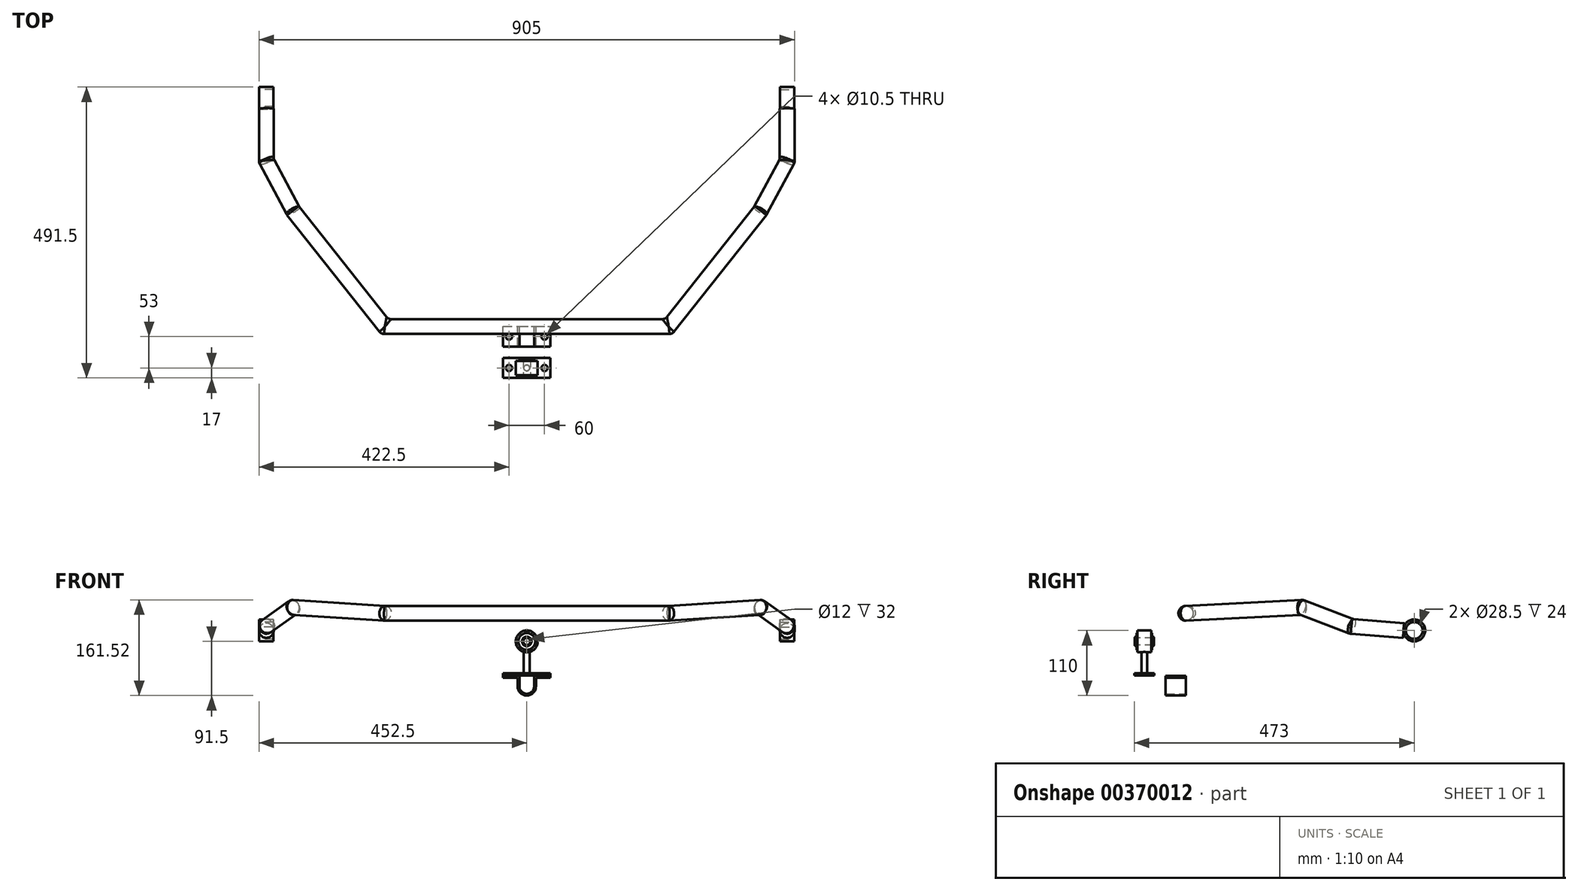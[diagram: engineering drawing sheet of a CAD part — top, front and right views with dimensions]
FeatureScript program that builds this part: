
annotation { "Feature Type Name" : "Feature", "Feature Type Description" : "" }
export const myFeature = defineFeature(function(context is Context, id is Id, definition is map)
    precondition{}
    {
        {
            var Q0;
            Q0=qCreatedBy(makeId("Top.planeOp"),FACE);
            var sketch = newSketch(context, id + "F0", { "sketchPlane" : qUnion([Q0])});
            skLineSegment(sketch, "E0", {"start": v(0, 0) * mm, "end": v(240, 0) * mm, "construction": true});
            skLineSegment(sketch, "E1", {"start": v(0, 0) * mm, "end": v(-240, 0) * mm, "construction": true});
            skLineSegment(sketch, "E2", {"start": v(0, 0) * mm, "end": v(0, 405) * mm, "construction": true});
            skPoint(sketch, "E3", {"position": v(0, 196) * mm});
            skPoint(sketch, "E4", {"position": v(0, 280) * mm});
            skPoint(sketch, "E5", {"position": v(0, 368) * mm});
            skLineSegment(sketch, "E6", {"start": v(0, 196) * mm, "end": v(395, 196) * mm, "construction": true});
            skLineSegment(sketch, "E7", {"start": v(0, 196) * mm, "end": v(-395, 196) * mm, "construction": true});
            skLineSegment(sketch, "E8", {"start": v(0, 368) * mm, "end": v(440, 368) * mm, "construction": true});
            skLineSegment(sketch, "E9", {"start": v(0, 368) * mm, "end": v(-440, 368) * mm, "construction": true});
            skLineSegment(sketch, "E10", {"start": v(395, 196) * mm, "end": v(240, 0) * mm, "construction": true});
            skLineSegment(sketch, "E11", {"start": v(-440, 368) * mm, "end": v(-395, 196) * mm, "construction": true});
            skLineSegment(sketch, "E12", {"start": v(-395, 196) * mm, "end": v(-240, 0) * mm, "construction": true});
            skPoint(sketch, "E13", {"position": v(440, 280) * mm});
            skLineSegment(sketch, "E14", {"start": v(395, 196) * mm, "end": v(440, 280) * mm, "construction": true});
            skLineSegment(sketch, "E15", {"start": v(440, 280) * mm, "end": v(440, 368) * mm, "construction": true});
            skSolve(sketch);
        }
        {
            var Q0;
            Q0=qCreatedBy(makeId("Right.planeOp"),FACE);
            var sketch = newSketch(context, id + "F1", { "sketchPlane" : qUnion([Q0])});
            skLineSegment(sketch, "E16.0", {"start": v(196, 0) * mm, "end": v(0, 0) * mm, "construction": true});
            skPoint(sketch, "E17", {"position": v(0, 47.5) * mm});
            skPoint(sketch, "E18", {"position": v(196, 57.5) * mm});
            skPoint(sketch, "E19", {"position": v(280, 0) * mm});
            skPoint(sketch, "E20", {"position": v(280, 25.5) * mm});
            skPoint(sketch, "E21", {"position": v(368, 0) * mm});
            skLineSegment(sketch, "E22", {"start": v(368, 0) * mm, "end": v(368, 18.5) * mm});
            skLineSegment(sketch, "E23", {"start": v(0, 47.5) * mm, "end": v(196, 57.5) * mm});
            skLineSegment(sketch, "E24", {"start": v(196, 57.5) * mm, "end": v(280, 25.5) * mm});
            skLineSegment(sketch, "E25", {"start": v(368, 18.5) * mm, "end": v(280, 25.5) * mm});
            skLineSegment(sketch, "E26", {"start": v(0, 47.5) * mm, "end": v(0, 0) * mm});
            skLineSegment(sketch, "E27", {"start": v(196, 57.5) * mm, "end": v(196, 0) * mm});
            skLineSegment(sketch, "E28", {"start": v(280, 25.5) * mm, "end": v(280, 0) * mm});
            skSolve(sketch);
        }
        {
            var Q0;
            Q0=qCreatedBy(makeId("Right.planeOp"),FACE);
            cPlane(context, id + "F2", {"entities" : qUnion([Q0]), "cplaneType" : CPlaneType.OFFSET, "offset" : 240 * mm, "width" : 150 * mm, "height" : 150 * mm});
        }
        {
            var Q0;
            Q0=qCreatedBy(id+"F2.planeOp",FACE);
            var sketch = newSketch(context, id + "F3", { "sketchPlane" : qUnion([Q0])});
            skLineSegment(sketch, "E29.0", {"start": v(0, 47.5) * mm, "end": v(0, 0) * mm});
            skSolve(sketch);
        }
        {
            var Q0;
            Q0=sQuery(id+"F3.wireOp",VERTEX,"E29.0.start");
            var Q1;
            Q1=sQuery(id+"F3.wireOp",VERTEX,"E29.0.end");
            var Q2;
            Q2=sQuery(id+"F0.wireOp",VERTEX,"E10.start");
            cPlane(context, id + "F4", {"entities" : qUnion([Q0, Q1, Q2]), "cplaneType" : CPlaneType.THREE_POINT, "offset" : 25 * mm, "width" : 150 * mm, "height" : 150 * mm});
        }
        {
            var Q0;
            Q0=qCreatedBy(id+"F4.planeOp",FACE);
            var sketch = newSketch(context, id + "F5", { "sketchPlane" : qUnion([Q0])});
            skLineSegment(sketch, "E30.0", {"start": v(-148.87, 47.5) * mm, "end": v(-148.87, 0) * mm});
            skLineSegment(sketch, "E31.0", {"start": v(-398.75, 0) * mm, "end": v(-148.87, 0) * mm, "construction": true});
            skLineSegment(sketch, "E32", {"start": v(-398.75, 0) * mm, "end": v(-398.75, 57.5) * mm});
            skLineSegment(sketch, "E33", {"start": v(-398.75, 57.5) * mm, "end": v(-148.87, 47.5) * mm});
            skSolve(sketch);
        }
        {
            var Q0;
            Q0=sQuery(id+"F5.wireOp",VERTEX,"E33.start");
            var Q1;
            Q1=sQuery(id+"F5.wireOp",VERTEX,"E32.start");
            var Q2;
            Q2=sQuery(id+"F0.wireOp",VERTEX,"E13");
            cPlane(context, id + "F6", {"entities" : qUnion([Q0, Q1, Q2]), "cplaneType" : CPlaneType.THREE_POINT, "offset" : 25 * mm, "width" : 150 * mm, "height" : 150 * mm});
        }
        {
            var Q0;
            Q0=qCreatedBy(id+"F6.planeOp",FACE);
            var sketch = newSketch(context, id + "F7", { "sketchPlane" : qUnion([Q0])});
            skLineSegment(sketch, "E34.0", {"start": v(-359.3, 0) * mm, "end": v(-359.3, 57.5) * mm});
            skLineSegment(sketch, "E35.0", {"start": v(-359.3, 0) * mm, "end": v(-454.6, 0) * mm, "construction": true});
            skLineSegment(sketch, "E36", {"start": v(-454.6, 0) * mm, "end": v(-454.6, 25.5) * mm});
            skLineSegment(sketch, "E37", {"start": v(-454.6, 25.5) * mm, "end": v(-359.3, 57.5) * mm});
            skSolve(sketch);
        }
        {
            var Q0;
            Q0=sQuery(id+"F7.wireOp",VERTEX,"E37.start");
            var Q1;
            Q1=sQuery(id+"F0.wireOp",VERTEX,"E13");
            var Q2;
            Q2=sQuery(id+"F0.wireOp",VERTEX,"E15.end");
            cPlane(context, id + "F8", {"entities" : qUnion([Q0, Q1, Q2]), "cplaneType" : CPlaneType.THREE_POINT, "offset" : 25 * mm, "width" : 150 * mm, "height" : 150 * mm});
        }
        {
            var Q0;
            Q0=qCreatedBy(id+"F8.planeOp",FACE);
            var sketch = newSketch(context, id + "F9", { "sketchPlane" : qUnion([Q0])});
            skLineSegment(sketch, "E38.0", {"start": v(-280, 0) * mm, "end": v(-280, 25.5) * mm});
            skLineSegment(sketch, "E39.0", {"start": v(-280, 0) * mm, "end": v(-368, 0) * mm, "construction": true});
            skLineSegment(sketch, "E40", {"start": v(-368, 0) * mm, "end": v(-368, 18.5) * mm});
            skLineSegment(sketch, "E41", {"start": v(-368, 18.5) * mm, "end": v(-280, 25.5) * mm});
            skSolve(sketch);
        }
        {
            var Q0;
            Q0=qCreatedBy(makeId("Front.planeOp"),FACE);
            var sketch = newSketch(context, id + "F10", { "sketchPlane" : qUnion([Q0])});
            skLineSegment(sketch, "E42", {"start": v(0, 0) * mm, "end": v(240, 0) * mm});
            skLineSegment(sketch, "E43.0", {"start": v(0, 47.5) * mm, "end": v(0, 0) * mm});
            skLineSegment(sketch, "E44", {"start": v(0, 47.5) * mm, "end": v(240, 47.5) * mm});
            skSolve(sketch);
        }
        {
            var Q0;
            Q0=qCreatedBy(makeId("Right.planeOp"),FACE);
            var sketch = newSketch(context, id + "F11", { "sketchPlane" : qUnion([Q0])});
            skCircle(sketch, "E45", {"center": v(0, 47.5) * mm, "radius": 12.5 * mm});
            skSolve(sketch);
        }
        {
            var Q0;
            Q0=makeQuery(id+"F11.imprint","IMPRINT",FACE,{"disambiguationData":[TD([[makeQuery(id+"F11.imprint","IMPRINT",EDGE,{"derivedFrom":sQuery(id+"F11.wireOp",EDGE,"E45")}),1.0]])]});
            var Q1;
            Q1=sQuery(id+"F10.wireOp",EDGE,"E44");
            var Q2;
            Q2=sQuery(id+"F5.wireOp",EDGE,"E33");
            var Q3;
            Q3=sQuery(id+"F7.wireOp",EDGE,"E37");
            var Q4;
            Q4=sQuery(id+"F9.wireOp",EDGE,"E41");
            sweep(context, id + "F12", {"profiles" : qUnion([Q0]), "path" : qUnion([Q1, Q2, Q3, Q4])});
        }
        {
            var Q0;
            Q0=qCreatedBy(id+"F8.planeOp",FACE);
            var sketch = newSketch(context, id + "F13", { "sketchPlane" : qUnion([Q0])});
            skLineSegment(sketch, "E46.0", {"start": v(-367, 6.04) * mm, "end": v(-369, 30.96) * mm});
            skPoint(sketch, "E47", {"position": v(-386, 18.5) * mm});
            skPoint(sketch, "E47.positionSnap0", {"position": v(-368, 18.5) * mm});
            skCircle(sketch, "E48", {"center": v(-386, 18.5) * mm, "radius": 18.5 * mm});
            skCircle(sketch, "E49", {"center": v(-386, 18.5) * mm, "radius": 14.25 * mm});
            skSolve(sketch);
        }
        {
            var Q0;
            Q0 = qSketchRegion(id + "F13", true);
            extrude(context, id + "F14", {"entities" : qUnion([Q0]), "operationType" : NewBodyOperationType.ADD, "endBound" : BoundingType.SYMMETRIC, "depth" : 24 * mm});
        }
        {
            var Q0;
            Q0=makeQuery(id+"F12.opSweep","MID_CAP_EDGE",EDGE,{"disambiguationData":[OSD([sQuery(id+"F5.wireOp",VERTEX,"E33.end"),sQuery(id+"F11.wireOp",EDGE,"E45")])],"capPos":1.0});
            var Q1;
            Q1=makeQuery(id+"F12.opSweep","MID_CAP_EDGE",EDGE,{"disambiguationData":[OSD([sQuery(id+"F7.wireOp",VERTEX,"E37.end"),sQuery(id+"F11.wireOp",EDGE,"E45")])],"capPos":2.0});
            var Q2;
            Q2=makeQuery(id+"F12.opSweep","MID_CAP_EDGE",EDGE,{"disambiguationData":[OSD([sQuery(id+"F9.wireOp",VERTEX,"E41.end"),sQuery(id+"F11.wireOp",EDGE,"E45")])],"capPos":3.0});
            fillet(context, id + "F15", {"entities" : qUnion([Q0, Q1, Q2]), "radius" : 10 * mm, "tangentPropagation" : true, "allowEdgeOverflow" : false});
        }
        {
            var Q0;
            Q0=makeQuery(id+"F12.opSweep","SWEPT_BODY",BODY,{"disambiguationData":[OSD([sQuery(id+"F9.wireOp",EDGE,"E41"),sQuery(id+"F11.wireOp",EDGE,"E45")])]});
            var Q1;
            Q1=qCreatedBy(makeId("Right.planeOp"),FACE);
            mirror(context, id + "F16", {"operationType" : NewBodyOperationType.ADD, "entities" : qUnion([Q0]), "mirrorPlane" : qUnion([Q1])});
        }
        {
            var Q0;
            Q0=qCreatedBy(makeId("Front.planeOp"),FACE);
            cPlane(context, id + "F17", {"entities" : qUnion([Q0]), "cplaneType" : CPlaneType.OFFSET, "offset" : 70 * mm, "width" : 150 * mm, "height" : 150 * mm});
        }
        {
            var Q0;
            Q0=qCreatedBy(id+"F17.planeOp",FACE);
            var sketch = newSketch(context, id + "F18", { "sketchPlane" : qUnion([Q0])});
            skCircle(sketch, "E50", {"center": v(0, 0) * mm, "radius": 18.5 * mm});
            skCircle(sketch, "E51", {"center": v(0, 0) * mm, "radius": 14.25 * mm});
            skSolve(sketch);
        }
        {
            var Q0;
            Q0 = qSketchRegion(id + "F18", true);
            extrude(context, id + "F19", {"entities" : qUnion([Q0]), "endBound" : BoundingType.SYMMETRIC, "depth" : 24 * mm});
        }
        {
            var Q0;
            Q0=qCreatedBy(id+"F17.planeOp",FACE);
            var sketch = newSketch(context, id + "F20", { "sketchPlane" : qUnion([Q0])});
            skPoint(sketch, "E52", {"position": v(0, -57.5) * mm});
            skLineSegment(sketch, "E53", {"start": v(0, -57.5) * mm, "end": v(40, -57.5) * mm});
            skLineSegment(sketch, "E54", {"start": v(40, -57.5) * mm, "end": v(40, -53.5) * mm});
            skLineSegment(sketch, "E55", {"start": v(40, -53.5) * mm, "end": v(-40, -53.5) * mm});
            skLineSegment(sketch, "E56", {"start": v(-40, -53.5) * mm, "end": v(-40, -57.5) * mm});
            skLineSegment(sketch, "E57", {"start": v(-40, -57.5) * mm, "end": v(0, -57.5) * mm});
            skSolve(sketch);
        }
        {
            var Q0;
            Q0 = qSketchRegion(id + "F20", true);
            extrude(context, id + "F21", {"entities" : qUnion([Q0]), "endBound" : BoundingType.SYMMETRIC, "depth" : 34 * mm});
        }
        {
            var Q0;
            Q0=qCreatedBy(id+"F17.planeOp",FACE);
            var sketch = newSketch(context, id + "F22", { "sketchPlane" : qUnion([Q0])});
            skCircle(sketch, "E58.0", {"center": v(0, 0) * mm, "radius": 18.5 * mm});
            skPoint(sketch, "E59", {"position": v(0, -18.5) * mm});
            skLineSegment(sketch, "E60.0", {"start": v(40, -53.5) * mm, "end": v(-40, -53.5) * mm});
            skLineSegment(sketch, "E61", {"start": v(0, -18.5) * mm, "end": v(0, -53.5) * mm});
            skLineSegment(sketch, "E62", {"start": v(0, -53.5) * mm, "end": v(5, -53.5) * mm});
            skLineSegment(sketch, "E63", {"start": v(5, -53.5) * mm, "end": v(5, -17.5) * mm});
            skLineSegment(sketch, "E64", {"start": v(5, -17.5) * mm, "end": v(0, -17.5) * mm});
            skLineSegment(sketch, "E65", {"start": v(0, -17.5) * mm, "end": v(0, -18.5) * mm});
            skSolve(sketch);
        }
        {
            var Q0;
            {var subQ0=sQuery(id+"F22.wireOp",EDGE,"E61");Q0=makeQuery(id+"F22.imprint","IMPRINT",FACE,{"disambiguationData":[TD([[makeQuery(id+"F22.imprint","IMPRINT",EDGE,{"derivedFrom":subQ0}),1.0]])]});}
            var Q1;
            Q1=sQuery(id+"F22.wireOp",EDGE,"E61");
            revolve(context, id + "F23", {"operationType" : NewBodyOperationType.ADD, "entities" : qUnion([Q0]), "axis" : qUnion([Q1]), "revolveType" : RevolveType.FULL});
        }
        {
            var Q0;
            Q0=qCreatedBy(makeId("Right.planeOp"),FACE);
            var sketch = newSketch(context, id + "F24", { "sketchPlane" : qUnion([Q0])});
            skLineSegment(sketch, "E66.0", {"start": v(-82, -14.25) * mm, "end": v(-82, 14.25) * mm});
            skLineSegment(sketch, "E67", {"start": v(-82, 0) * mm, "end": v(-57, 0) * mm});
            skPoint(sketch, "E67.endSnap0", {"position": v(-82, 0) * mm});
            skLineSegment(sketch, "E68", {"start": v(-57, 0) * mm, "end": v(-57, 14.25) * mm});
            skLineSegment(sketch, "E69", {"start": v(-57, 14.25) * mm, "end": v(-83, 14.25) * mm});
            skLineSegment(sketch, "E70", {"start": v(-83, 14.25) * mm, "end": v(-83, 0) * mm});
            skLineSegment(sketch, "E71", {"start": v(-83, 0) * mm, "end": v(-82, 0) * mm});
            skPoint(sketch, "E72", {"position": v(-70, 0) * mm});
            skPoint(sketch, "E72.positionSnap0", {"position": v(-70, 14.25) * mm});
            skLineSegment(sketch, "E73", {"start": v(-70, 0) * mm, "end": v(-86, 0) * mm});
            skLineSegment(sketch, "E74", {"start": v(-86, 0) * mm, "end": v(-86, 6) * mm});
            skLineSegment(sketch, "E75", {"start": v(-86, 6) * mm, "end": v(-54, 6) * mm});
            skLineSegment(sketch, "E76", {"start": v(-54, 6) * mm, "end": v(-54, 0) * mm});
            skLineSegment(sketch, "E77", {"start": v(-54, 0) * mm, "end": v(-57, 0) * mm});
            skLineSegment(sketch, "E78", {"start": v(-86, 6) * mm, "end": v(-86, 8) * mm});
            skLineSegment(sketch, "E79", {"start": v(-86, 8) * mm, "end": v(-83, 8) * mm});
            skLineSegment(sketch, "E80", {"start": v(-54, 6) * mm, "end": v(-54, 8) * mm});
            skLineSegment(sketch, "E81", {"start": v(-54, 8) * mm, "end": v(-57, 8) * mm});
            skSolve(sketch);
        }
        {
            var Q0;
            {var subQ4=sQuery(id+"F24.wireOp",EDGE,"E80");Q0=makeQuery(id+"F24.imprint","IMPRINT",FACE,{"disambiguationData":[TD([[makeQuery(id+"F24.imprint","IMPRINT",EDGE,{"derivedFrom":subQ4}),1.0]])]});}
            var Q1;
            {var subQ4=sQuery(id+"F24.wireOp",EDGE,"E78");Q1=makeQuery(id+"F24.imprint","IMPRINT",FACE,{"disambiguationData":[TD([[makeQuery(id+"F24.imprint","IMPRINT",EDGE,{"derivedFrom":subQ4}),-1.0]])]});}
            var Q2;
            {var subQ0=sQuery(id+"F24.wireOp",EDGE,"E69");var subQ6=sQuery(id+"F24.wireOp",EDGE,"E66.0");var subQ7=makeQuery(id+"F24.imprint","INTERSECT",VERTEX,{"derivedFrom":[subQ6,subQ0]});Q2=makeQuery(id+"F24.imprint","IMPRINT",FACE,{"disambiguationData":[TD([[makeQuery(id+"F24.imprint","IMPRINT",EDGE,{"disambiguationData":[TD([[subQ7,1.0]])],"derivedFrom":subQ6}),-1.0]])]});}
            var Q3;
            {var subQ4=sQuery(id+"F24.wireOp",EDGE,"E69");var subQ6=sQuery(id+"F24.wireOp",EDGE,"E66.0");var subQ7=makeQuery(id+"F24.imprint","INTERSECT",VERTEX,{"derivedFrom":[subQ6,subQ4]});Q3=makeQuery(id+"F24.imprint","IMPRINT",FACE,{"disambiguationData":[TD([[makeQuery(id+"F24.imprint","IMPRINT",EDGE,{"disambiguationData":[TD([[subQ7,1.0]])],"derivedFrom":subQ6}),1.0]])]});}
            var Q4;
            Q4=sQuery(id+"F24.wireOp",EDGE,"E67");
            revolve(context, id + "F25", {"operationType" : NewBodyOperationType.ADD, "entities" : qUnion([Q0, Q1, Q2, Q3]), "axis" : qUnion([Q4]), "revolveType" : RevolveType.FULL});
        }
        {
            var Q0;
            Q0=makeQuery(id+"F21.opExtrude","SWEPT_FACE",FACE,{"disambiguationData":[OSD([sQuery(id+"F20.wireOp",EDGE,"E53"),sQuery(id+"F20.wireOp",EDGE,"E57")])]});
            var sketch = newSketch(context, id + "F26", { "sketchPlane" : qUnion([Q0])});
            skLineSegment(sketch, "E82.0", {"start": v(40, 87) * mm, "end": v(40, 53) * mm});
            skLineSegment(sketch, "E83.0", {"start": v(-40, 87) * mm, "end": v(-40, 53) * mm});
            skPoint(sketch, "E84", {"position": v(-30, 70) * mm});
            skPoint(sketch, "E84.positionSnap0", {"position": v(-40, 70) * mm});
            skPoint(sketch, "E85", {"position": v(30, 70) * mm});
            skPoint(sketch, "E85.positionSnap0", {"position": v(40, 70) * mm});
            skCircle(sketch, "E86", {"center": v(-30, 70) * mm, "radius": 5.25 * mm});
            skCircle(sketch, "E87", {"center": v(30, 70) * mm, "radius": 5.25 * mm});
            skSolve(sketch);
        }
        {
            var Q0;
            Q0 = qSketchRegion(id + "F26", true);
            extrude(context, id + "F27", {"entities" : qUnion([Q0]), "operationType" : NewBodyOperationType.REMOVE, "oppositeDirection" : true, "depth" : 25 * mm});
        }
        {
            var Q0;
            Q0=makeQuery(id+"F25.opRevolve","SWEPT_EDGE",EDGE,{"disambiguationData":[OSD([sQuery(id+"F24.wireOp",EDGE,"E78"),sQuery(id+"F24.wireOp",EDGE,"E79")])]});
            var Q1;
            Q1=makeQuery(id+"F25.opRevolve","SWEPT_EDGE",EDGE,{"disambiguationData":[OSD([sQuery(id+"F24.wireOp",EDGE,"E80"),sQuery(id+"F24.wireOp",EDGE,"E81")])]});
            chamfer(context, id + "F28", {"entities" : qUnion([Q0, Q1]), "width" : 1 * mm, "tangentPropagation" : true});
        }
        {
            var Q0;
            Q0=qCreatedBy(makeId("Front.planeOp"),FACE);
            var sketch = newSketch(context, id + "F29", { "sketchPlane" : qUnion([Q0])});
            skLineSegment(sketch, "E88.0", {"start": v(-40, -57.5) * mm, "end": v(40, -57.5) * mm});
            skPoint(sketch, "E89", {"position": v(0, -58.5) * mm});
            skPoint(sketch, "E89.positionSnap0", {"position": v(0, -57.5) * mm});
            skLineSegment(sketch, "E90", {"start": v(-40, -58.5) * mm, "end": v(-12.5, -58.5) * mm});
            skArc(sketch, "E91", {"start": v(-12.5, -76) * mm, "mid": v(0, -88.5) * mm, "end": v(12.5, -76) * mm});
            skPoint(sketch, "E92", {"position": v(12.5, -76) * mm});
            skPoint(sketch, "E93", {"position": v(-12.5, -76) * mm});
            skLineSegment(sketch, "E94", {"start": v(-12.5, -76) * mm, "end": v(-12.5, -58.5) * mm});
            skLineSegment(sketch, "E95", {"start": v(12.5, -76) * mm, "end": v(12.5, -58.5) * mm});
            skLineSegment(sketch, "E96.trimOffspring", {"start": v(12.5, -58.5) * mm, "end": v(40, -58.5) * mm});
            skLineSegment(sketch, "E97.0", {"start": v(15.5, -61.5) * mm, "end": v(40, -61.5) * mm});
            skLineSegment(sketch, "E97.1", {"start": v(-40, -61.5) * mm, "end": v(-15.5, -61.5) * mm});
            skLineSegment(sketch, "E97.2", {"start": v(-15.5, -76) * mm, "end": v(-15.5, -61.5) * mm});
            skArc(sketch, "E97.3", {"start": v(-15.5, -76) * mm, "mid": v(0, -91.5) * mm, "end": v(15.5, -76) * mm});
            skLineSegment(sketch, "E97.4", {"start": v(15.5, -76) * mm, "end": v(15.5, -61.5) * mm});
            skLineSegment(sketch, "E98", {"start": v(-40, -58.5) * mm, "end": v(-40, -61.5) * mm});
            skLineSegment(sketch, "E99", {"start": v(40, -58.5) * mm, "end": v(40, -61.5) * mm});
            skSolve(sketch);
        }
        {
            var Q0;
            Q0 = qSketchRegion(id + "F29", true);
            extrude(context, id + "F30", {"entities" : qUnion([Q0]), "depth" : 34 * mm});
        }
        {
            var Q0;
            Q0=makeQuery(id+"F30.opExtrude","SWEPT_FACE",FACE,{"disambiguationData":[OSD([sQuery(id+"F29.wireOp",EDGE,"E90")])]});
            var sketch = newSketch(context, id + "F31", { "sketchPlane" : qUnion([Q0])});
            skPoint(sketch, "E100", {"position": v(-30, -17) * mm});
            skPoint(sketch, "E100.positionSnap0", {"position": v(-40, -17) * mm});
            skPoint(sketch, "E101", {"position": v(30, -17) * mm});
            skCircle(sketch, "E102", {"center": v(30, -17) * mm, "radius": 5.25 * mm});
            skCircle(sketch, "E103", {"center": v(-30, -17) * mm, "radius": 5.25 * mm});
            skSolve(sketch);
        }
        {
            var Q0;
            Q0 = qSketchRegion(id + "F31", true);
            extrude(context, id + "F32", {"entities" : qUnion([Q0]), "operationType" : NewBodyOperationType.REMOVE, "oppositeDirection" : true, "depth" : 25 * mm});
        }
    });
